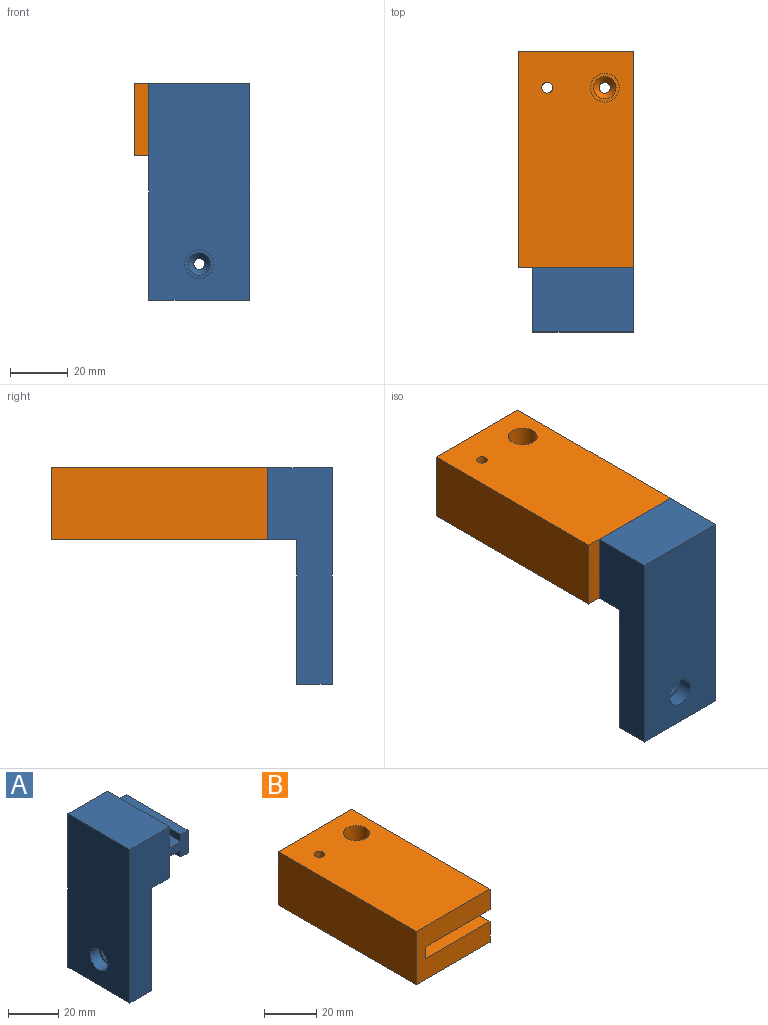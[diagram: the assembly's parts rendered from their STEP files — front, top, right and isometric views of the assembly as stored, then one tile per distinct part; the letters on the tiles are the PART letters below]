
ASSEMBLY  parts=2 mates=1
PART A: 20 faces, bbox 32.8x35x75 mm
  f0: plane 75x32.8mm, normal (0,1,0), area 1242.5mm2, adj f2,f3,f4,f5,f6,f7,f8,f9
  f1: plane 75x32.8mm, normal (0,-1,0), area 1242.5mm2, adj f2,f3,f4,f5,f6,f7,f8,f9
  f2: plane 35x10.5mm, normal (1,0,0), area 367.5mm2, adj f0,f1,f3,f8
  f3: plane 35x22.3mm, normal (0,0,1), area 780.5mm2, adj f0,f1,f2,f15
  f4: plane 35x12.3mm, normal (0,0,-1), area 430.5mm2, adj f0,f1,f5,f15
  f5: plane 50x35mm, normal (1,0,0), area 1738.7mm2, adj f0,f1,f4,f6,f18
  f6: plane 35x10mm, normal (0,0,-1), area 350mm2, adj f0,f1,f5,f7
  f7: plane 35x10.5mm, normal (1,0,0), area 367.5mm2, adj f0,f1,f6,f14
  f8: plane 35x6.5mm, normal (0,0,1), area 227.5mm2, adj f0,f1,f2,f9
  f9: plane 35x3.5mm, normal (-1,0,0), area 122.5mm2, adj f0,f1,f8,f10
  f10: plane 35x4mm, normal (0,0,1), area 140mm2, adj f0,f1,f9,f11
  f11: plane 35x11mm, normal (1,0,0), area 385mm2, adj f0,f1,f10,f12
  f12: plane 35x4mm, normal (0,0,-1), area 140mm2, adj f0,f1,f11,f13
  f13: plane 35x3.5mm, normal (-1,0,0), area 122.5mm2, adj f0,f1,f12,f14
  f14: plane 35x6.5mm, normal (0,0,-1), area 227.5mm2, adj f0,f1,f7,f13
  f15: plane 75x35mm, normal (-1,0,0), area 2546.5mm2, adj f0,f1,f3,f4,f17
  f16: plane 10x10mm, normal (-1,0,0), area 30.8mm2, adj f17,f19
  f17: cylinder r=5mm len=10mm, axis (-1,0,0), area 159.6mm2, adj f15,f16
  f18: cylinder r=1.9mm len=4.92mm, axis (-1,0,0), area 58.7mm2, adj f5,f19
  f19: cone r=1.9mm half-angle=41deg, axis (-1,0,0), area 55.5mm2, adj f16,f18
PART B: 22 faces, bbox 40x75x25 mm
  f0: plane 75x25mm, normal (-1,0,0), area 1875mm2, adj f1,f3,f4,f5
  f1: plane 40x25mm, normal (0,-1,0), area 807.5mm2, adj f0,f2,f4,f5,f6,f7,f13
  f2: plane 75x25mm, normal (1,0,0), area 1776mm2, adj f1,f3,f4,f5,f6,f7,f8,f9
  f3: plane 40x25mm, normal (0,1,0), area 1000mm2, adj f0,f2,f4,f5
  f4: plane 75x40mm, normal (0,0,1), area 2910.1mm2, adj f0,f1,f2,f3,f16,f20
  f5: plane 75x40mm, normal (0,0,-1), area 2910.1mm2, adj f0,f1,f2,f3,f14,f18
  f6: plane 35x5.5mm, normal (0,0,-1), area 192.5mm2, adj f1,f2,f12,f13
  f7: plane 35x5.5mm, normal (0,0,1), area 192.5mm2, adj f1,f2,f8,f13
  f8: plane 35x3.5mm, normal (0,1,0), area 122.5mm2, adj f2,f7,f9,f13
  f9: plane 35x5.5mm, normal (0,0,1), area 192.5mm2, adj f2,f8,f10,f13
  f10: plane 35x12.5mm, normal (0,-1,0), area 437.5mm2, adj f2,f9,f11,f13
  f11: plane 35x5.5mm, normal (0,0,-1), area 192.5mm2, adj f2,f10,f12,f13
  f12: plane 35x3.5mm, normal (0,1,0), area 122.5mm2, adj f2,f6,f11,f13
  f13: plane 12.5x11mm, normal (1,0,0), area 99mm2, adj f1,f6,f7,f8,f9,f10,f11,f12
  f14: cylinder r=5mm len=19.05mm, axis (0,0,-1), area 598.5mm2, adj f5,f15
  f15: plane 10x10mm, normal (0,0,-1), area 30.8mm2, adj f14,f21
  f16: cylinder r=5mm len=19.05mm, axis (0,0,1), area 598.5mm2, adj f4,f17
  f17: plane 10x10mm, normal (0,0,1), area 30.8mm2, adj f16,f19
  f18: cylinder r=1.9mm len=3.8mm, axis (0,0,1), area 43.5mm2, adj f5,f19
  f19: cone r=1.9mm half-angle=41deg, axis (0,0,1), area 55.5mm2, adj f17,f18
  f20: cylinder r=1.9mm len=3.8mm, axis (0,0,-1), area 43.5mm2, adj f4,f21
  f21: cone r=1.9mm half-angle=41deg, axis (0,0,-1), area 55.5mm2, adj f15,f20
PLACE A rot(axis=(0,0,1),90deg) t=(-119.97,-29.93,42.69)mm
PLACE B t=(4.38,5.07,17.69)mm
MATE fastened A.f2 <-> B.f1  axis (0,1,0) through (44.38,5.07,42.69)mm
